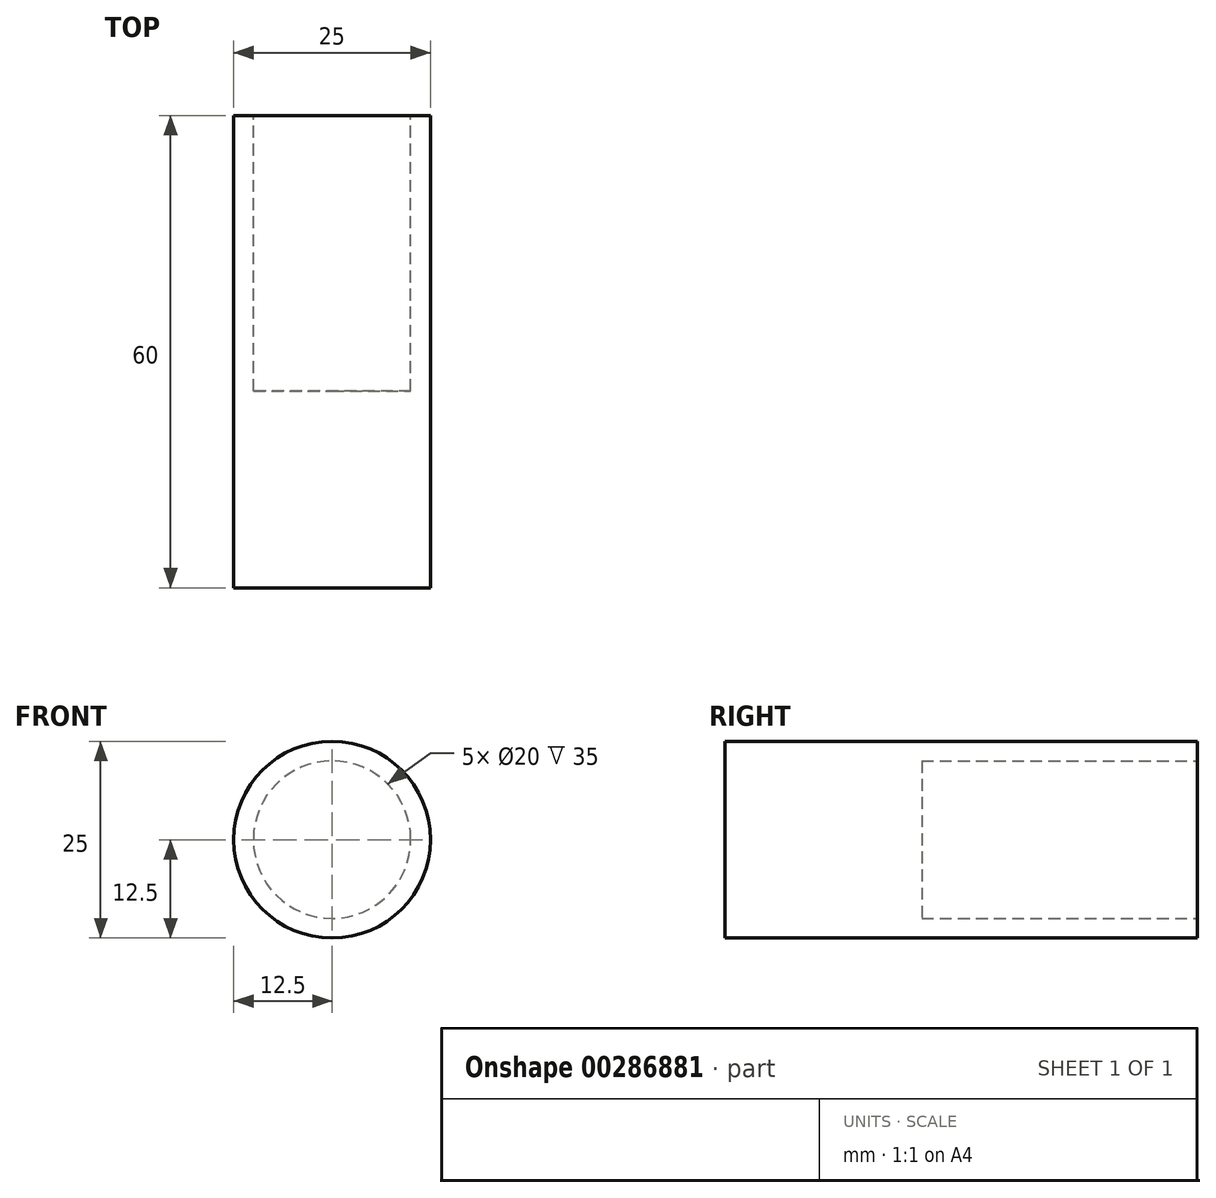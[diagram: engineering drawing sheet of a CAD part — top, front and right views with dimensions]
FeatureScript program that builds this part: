
annotation { "Feature Type Name" : "Feature", "Feature Type Description" : "" }
export const myFeature = defineFeature(function(context is Context, id is Id, definition is map)
    precondition{}
    {
        {
            var Q0;
            Q0=qCreatedBy(makeId("Front.planeOp"),FACE);
            var sketch = newSketch(context, id + "F0", { "sketchPlane" : qUnion([Q0])});
            skCircle(sketch, "E0", {"center": v(0, 0) * mm, "radius": 12.5 * mm});
            skSolve(sketch);
        }
        {
            var Q0;
            Q0=qSketchRegion(id+"F0",true);
            extrude(context, id + "F1", {"entities" : qUnion([Q0]), "depth" : 60 * mm});
        }
        {
            var Q0;
            Q0=makeQuery(id+"F1.opExtrude","CAP_FACE",FACE,{"disambiguationData":[OSD([sQuery(id+"F0.wireOp",EDGE,"E0")])],"isStart":true});
            var sketch = newSketch(context, id + "F2", { "sketchPlane" : qUnion([Q0])});
            skCircle(sketch, "E1", {"center": v(0, 0) * mm, "radius": 10 * mm});
            skSolve(sketch);
        }
        {
            var Q0;
            Q0=qSketchRegion(id+"F2",true);
            extrude(context, id + "F3", {"entities" : qUnion([Q0]), "operationType" : NewBodyOperationType.REMOVE, "oppositeDirection" : true, "depth" : 35 * mm});
        }
    });
